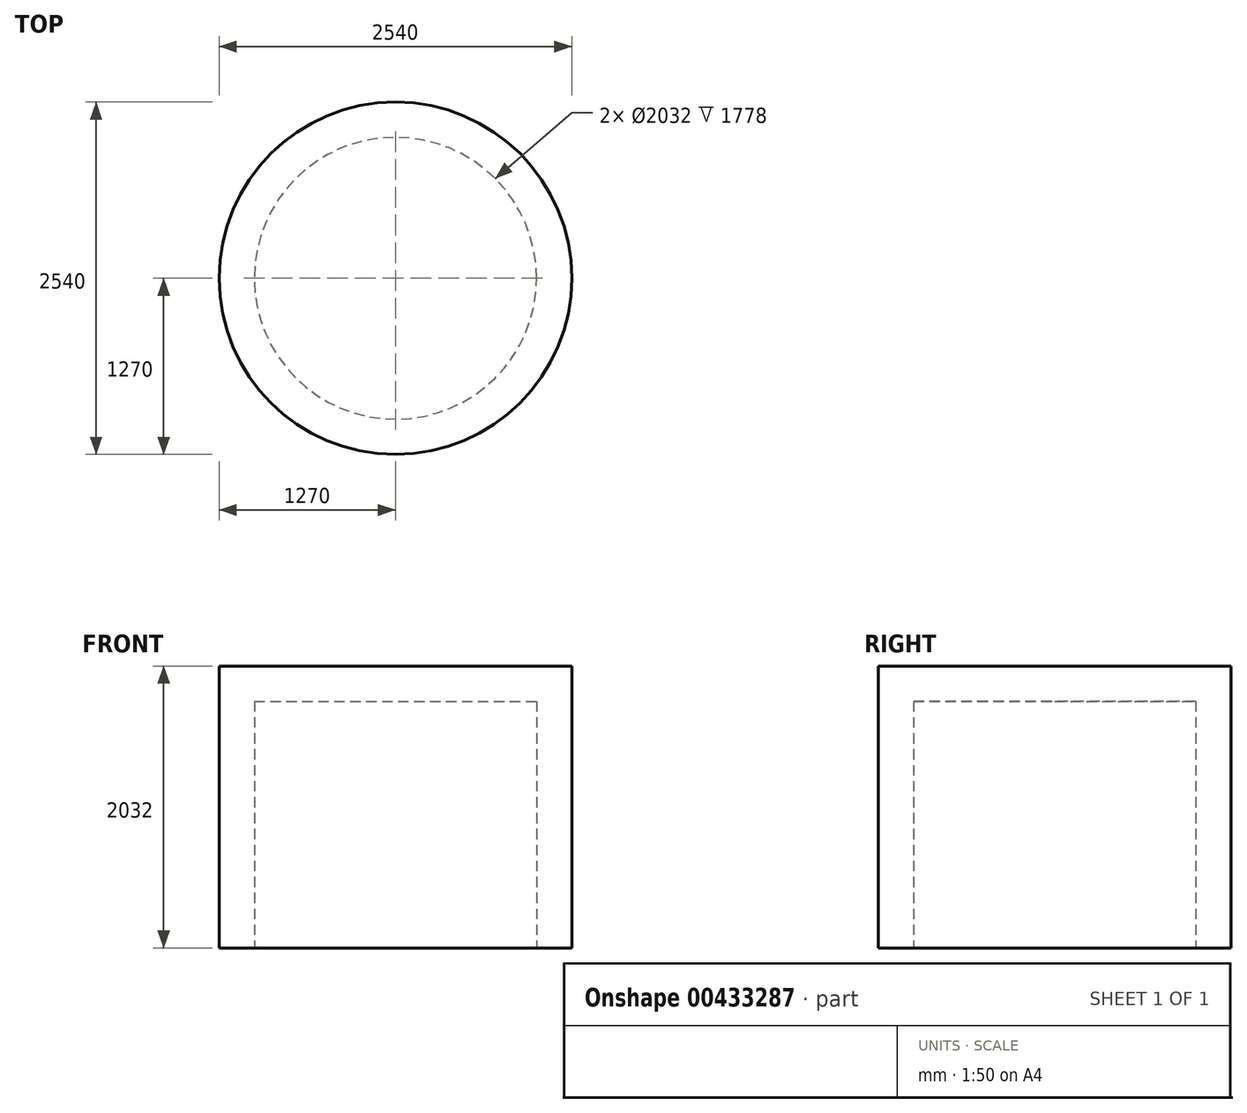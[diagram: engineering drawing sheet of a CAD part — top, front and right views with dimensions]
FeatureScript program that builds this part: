
annotation { "Feature Type Name" : "Feature", "Feature Type Description" : "" }
export const myFeature = defineFeature(function(context is Context, id is Id, definition is map)
    precondition{}
    {
        {
            var Q0;
            Q0=qCreatedBy(makeId("Top.planeOp"),FACE);
            var sketch = newSketch(context, id + "F0", { "sketchPlane" : qUnion([Q0])});
            skCircle(sketch, "E0", {"center": v(0, 0) * mm, "radius": 1270 * mm});
            skSolve(sketch);
        }
        {
            var Q0;
            Q0=makeQuery(id+"F0.imprint","IMPRINT",FACE,{"disambiguationData":[TD([[makeQuery(id+"F0.imprint","IMPRINT",EDGE,{"derivedFrom":sQuery(id+"F0.wireOp",EDGE,"E0")}),1.0]])]});
            extrude(context, id + "F1", {"entities" : qUnion([Q0]), "oppositeDirection" : true, "depth" : 2032 * mm});
        }
        {
            var Q0;
            Q0=makeQuery(id+"F1.opExtrude","CAP_FACE",FACE,{"disambiguationData":[OSD([sQuery(id+"F0.wireOp",EDGE,"E0")])],"isStart":false});
            var sketch = newSketch(context, id + "F2", { "sketchPlane" : qUnion([Q0])});
            skCircle(sketch, "E1", {"center": v(0, 0) * mm, "radius": 1016 * mm});
            skSolve(sketch);
        }
        {
            var Q0;
            Q0=makeQuery(id+"F2.imprint","IMPRINT",FACE,{"disambiguationData":[TD([[makeQuery(id+"F2.imprint","IMPRINT",EDGE,{"derivedFrom":sQuery(id+"F2.wireOp",EDGE,"E1")}),1.0]])]});
            extrude(context, id + "F3", {"entities" : qUnion([Q0]), "operationType" : NewBodyOperationType.REMOVE, "oppositeDirection" : true, "depth" : 1778 * mm});
        }
    });
